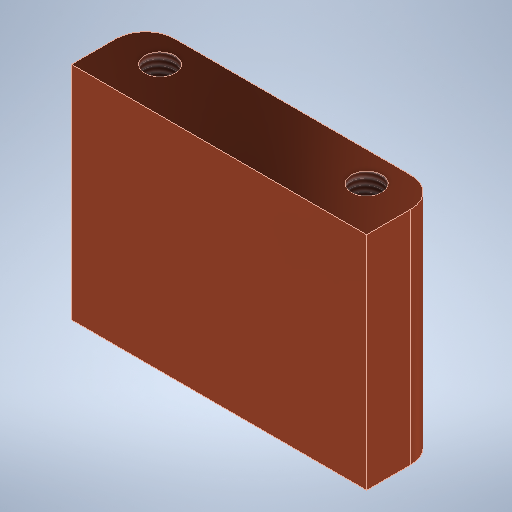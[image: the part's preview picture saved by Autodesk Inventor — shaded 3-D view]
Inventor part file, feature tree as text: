
AUTODESK INVENTOR PART (.ipt)
format: ipt  version: 2025.1 (Build 291241000, 241)  size: 223,232 bytes
history: native  units: mm
features: sketch x2, extrude x1, fillet x1, hole x1, projected_geometry x1
ambient origin geometry x8: Origin, YZ Plane, XZ Plane, XY Plane, X Axis, Y Axis, Z Axis, Center Point
bodies: Solid1 (feature_tree)
feature tree (6):
  extrude  "Extrusion1"  Depth=10.0mm
  fillet  "Fillet1"  Radius=30.0mm
  hole  "Hole1"  [1 undecoded]
  sketch  "Sketch1"  dims[d0=40.0mm d1=10.0mm d2=30.0mm d3=0.0mm]
  sketch  "Sketch2"  dims[d4=4.0mm d5=4.134mm d6=10.0mm d7=4.0mm d8=2.0mm d9=90.0deg d10=8.0mm d11=0.0mm d12=28.0mm d13=14.0mm]
  projected_geometry  "Projected Loop1"
note: 1 required parameter value undecoded (feature->parameter linkage not recoverable at this tier; creation-order binding heuristic only, values carry confidence <= 0.55)
